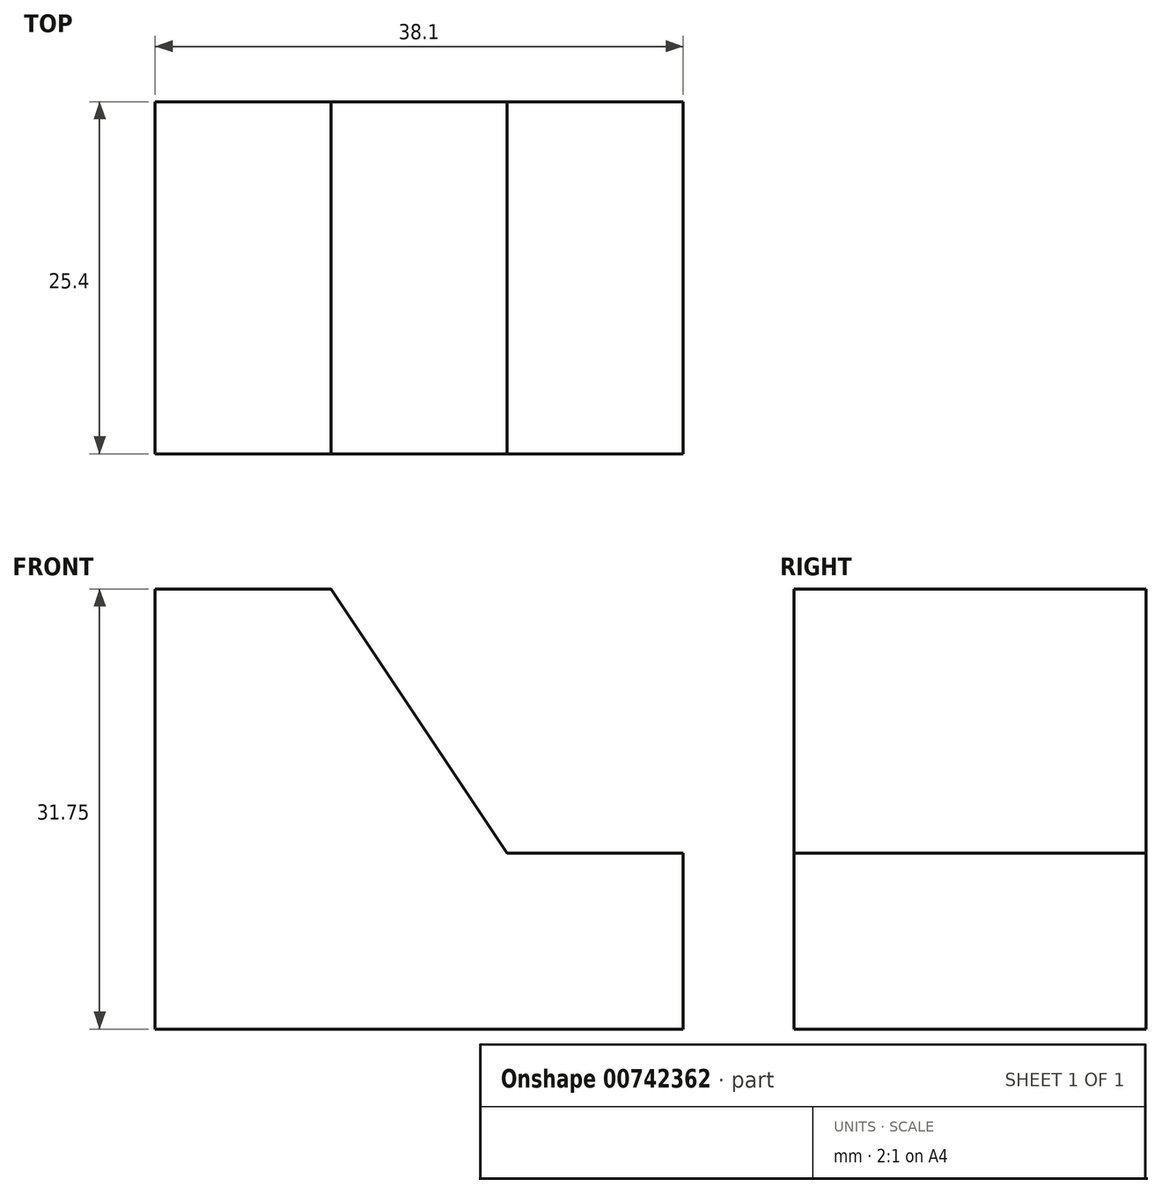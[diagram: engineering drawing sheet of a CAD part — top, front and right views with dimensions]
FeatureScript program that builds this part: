
annotation { "Feature Type Name" : "Feature", "Feature Type Description" : "" }
export const myFeature = defineFeature(function(context is Context, id is Id, definition is map)
    precondition{}
    {
        {
            var Q0;
            Q0=qCreatedBy(makeId("Front.planeOp"),FACE);
            var sketch = newSketch(context, id + "F0", { "sketchPlane" : qUnion([Q0])});
            skLineSegment(sketch, "E0", {"start": v(0, 31.75) * mm, "end": v(0, 0) * mm});
            skLineSegment(sketch, "E1", {"start": v(0, 0) * mm, "end": v(-38.1, 0) * mm});
            skLineSegment(sketch, "E2", {"start": v(-38.1, 0) * mm, "end": v(-38.1, 31.75) * mm});
            skLineSegment(sketch, "E3", {"start": v(-38.1, 31.75) * mm, "end": v(0, 31.75) * mm});
            skSolve(sketch);
        }
        {
            var Q0;
            Q0 = qSketchRegion(id + "F0", true);
            extrude(context, id + "F1", {"entities" : qUnion([Q0]), "depth" : 25.4 * mm, "offsetDistance" : 25.4 * mm});
        }
        {
            var Q0;
            Q0=makeQuery(id+"F1.opExtrude","CAP_FACE",FACE,{"disambiguationData":[OSD([sQuery(id+"F0.wireOp",EDGE,"E0"),sQuery(id+"F0.wireOp",EDGE,"E1"),sQuery(id+"F0.wireOp",EDGE,"E2"),sQuery(id+"F0.wireOp",EDGE,"E3")])],"isStart":false});
            var sketch = newSketch(context, id + "F2", { "sketchPlane" : qUnion([Q0])});
            skLineSegment(sketch, "E4", {"start": v(-25.4, 31.75) * mm, "end": v(-12.7, 12.7) * mm});
            skLineSegment(sketch, "E5", {"start": v(-12.7, 12.7) * mm, "end": v(0, 12.7) * mm});
            skLineSegment(sketch, "E6", {"start": v(0, 12.7) * mm, "end": v(0, 31.75) * mm});
            skLineSegment(sketch, "E7", {"start": v(0, 31.75) * mm, "end": v(-25.4, 31.75) * mm});
            skSolve(sketch);
        }
        {
            var Q0;
            Q0=makeQuery(id+"F2.imprint","IMPRINT",FACE,{"disambiguationData":[TD([[makeQuery(id+"F2.imprint","IMPRINT",EDGE,{"derivedFrom":sQuery(id+"F2.wireOp",EDGE,"E4")}),1.0]])]});
            extrude(context, id + "F3", {"entities" : qUnion([Q0]), "operationType" : NewBodyOperationType.REMOVE, "endBound" : BoundingType.THROUGH_ALL, "oppositeDirection" : true, "depth" : 25.4 * mm, "offsetDistance" : 25.4 * mm});
        }
    });
